# Revit family: P200635WX-135c_WUW55X24HZ
name_source: partatom
category: Specialty Equipment
units: mm (PartAtom-declared; Revit-internal decimal feet)

## family parameters
Always vertical = Yes
Cut with Voids When Loaded = No
Enable Cutting in Views = No
Maintain Annotation Orientation = No
Part Type = Normal
Room Calculation Point = No
Round Connector Dimension = Use Diameter
Shared = No
Work Plane-Based = No

## types (1)
- WUW55X24HZ
    Amps = 20 A
    Back Panel Material = ARCAT - Metal - Steel - Black
    Body Material = ARCAT - Metal - Steel - Black
    Clearance Material = ARCAT - Clearance
    Default Elevation = 0"
    Depth = 23 3/4"
    Description = 24-inch Wide Undercounter Wine Center with 46-Bottle Wine Storage
Cellier sous le comptoir, 24 po, 46 bouteilles
    Display Panel Material = ARCAT - Metal - Cast Iron 1/4" Plate
    Door Material = ARCAT - Metal - Steel - Stainless
    Family Name = Wine Cellar
    Feature 1 = Wine Storage
Rangement pour le vin
    Feature 2 = Dual-Temperature Controlled Zone
Deux zones à température contrôlée
    Feature 3 = LED Interior Lighting
Éclairage intérieur à DEL
    Glass Material = ARCAT - Glass - Tempered - Black
    Handle Material = ARCAT - Metal - Steel - Grey
    Height = 34 5/8"
    Leg Material = ARCAT - Plastic - Black
    Manufacturer = Whirlpool
    Model = WUW55X24HZ
    Rack Material = ARCAT - Metal - Steel - Stainless
    Voltage = 115 V
    Width = 23 13/16"

## geometry (parser evidence)
native form markers: Sweep x4
no freeform markers — native parametric forms only
